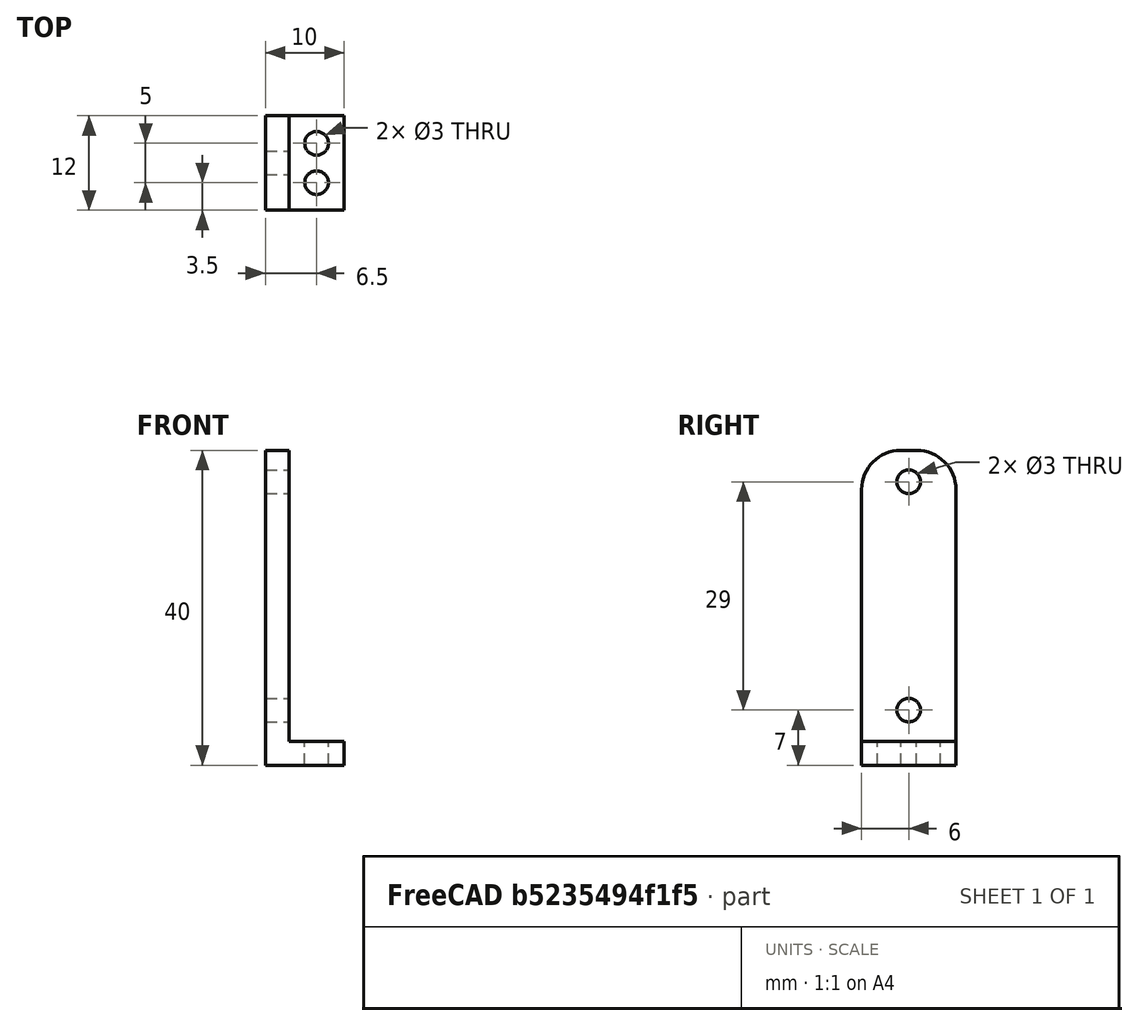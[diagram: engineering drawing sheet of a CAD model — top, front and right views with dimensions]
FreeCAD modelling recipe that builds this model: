
FCSTD DOCUMENT  (FreeCAD 0.16R6700 (Git))
Label: IR sensor bracket
License: All rights reserved
LicenseURL: http://en.wikipedia.org/wiki/All_rights_reserved
objects: Part::Cylinder×4, Part::Cut×4, Part::Box×2, Part::Fillet×1, Part::MultiFuse×1
note: 12 computed .brp shape members not serialized (recipe doc carries the construction recipe); baked Part::Feature solids carry a one-line shape summary decoded from their .brp

FEATURE [Part::Box] Box  label="Cube"
  Height = 3
  Length = 10
  Width = 12
FEATURE [Part::Box] Box001  label="Cube001"
  Height = 40
  Length = 3
  Width = 12
FEATURE [Part::Cylinder] Cylinder
  Angle = 360
  Height = 10
  Placement = pos=(6.5,3.5,0) rot=(0,0,1;0rad)
  Radius = 1.5
FEATURE [Part::Cut] Cut
  Base = -> Box
  Tool = -> Cylinder
FEATURE [Part::Cylinder] Cylinder001
  Angle = 360
  Height = 10
  Placement = pos=(6.5,8.5,0) rot=(0,0,1;0rad)
  Radius = 1.5
FEATURE [Part::Cut] Cut001
  Base = -> Cut
  Tool = -> Cylinder001
FEATURE [Part::Fillet] Fillet
  Base = -> Box001
  Edges = 2 edges r=5: [Edge10,Edge12]
FEATURE [Part::Cylinder] Cylinder002
  Angle = 360
  Height = 10
  Placement = pos=(0,6,7) rot=(0,1,0;1.5708rad)
  Radius = 1.5
FEATURE [Part::Cut] Cut002
  Base = -> Fillet
  Tool = -> Cylinder002
FEATURE [Part::Cylinder] Cylinder003
  Angle = 360
  Height = 10
  Placement = pos=(0,6,36) rot=(0,1,0;1.5708rad)
  Radius = 1.5
FEATURE [Part::Cut] Cut003
  Base = -> Cut002
  Tool = -> Cylinder003
FEATURE [Part::MultiFuse] Fusion
  Shapes = -> [Cut001,Cut003]
